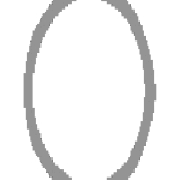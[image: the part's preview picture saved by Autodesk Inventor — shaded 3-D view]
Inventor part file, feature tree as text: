
AUTODESK INVENTOR PART (.ipt)
format: ipt  version: 2021 (Build 250183000, 183)  size: 110,080 bytes
history: native  units: in
note: dims shown in document units (in); Inventor stores cm internally (conversion verified against a paired STEP export)
features: other x4, sketch x3, plane x1
ambient origin geometry x8: Origin, YZ Plane, XZ Plane, XY Plane, X Axis, Y Axis, Z Axis, Center Point
bodies: Solid1 (feature_tree), Body (feature_tree)
feature tree (8):
  other  "Driven Length"
  other  "Frame Generator"
  other  "Start Plane"
  other  "End Plane"
  sketch  "Sketch"  dims[d2=20.6216in d4=-0.0in d5=20.6216in d6=0.12in d7=0.0in d8=90.0deg d9=20.6216in]
  sketch  "Sketch2"  dims[d0=1.0in]
  plane  "Work Plane3"
  sketch  "Sketch3"  dims[d1=0.065in]
